# Revit family: Genie_Site_Telehandler_GTH12561
name_source: partatom
category: Site
units: mm (PartAtom-declared; Revit-internal decimal feet)

## family parameters
Always vertical = Yes
Cut with Voids When Loaded = No
OmniClass Number = 23.50.85.17
OmniClass Title = Telescoping Platforms
Part Type = Normal
Round Connector Dimension = Use Diameter
Shared = No
Work Plane-Based = No

## types (1)
- GTH-1256
    Assembly Code = E1030900
    AssetType = Fixed
    BIMObjectName = Genie_Site_Telehandler_GTH1256
    ClassificationName = Uniclass2015
    ClassificationValue = Pr_65_80_47_95
    Color = Grey & Blue
    Cost = 0 $
    Description = The Genie® GTH™-1256 telehandler delivers productivity with a large lifting capacity, high reach and compact maneuverability. And, this telehandler is built to perform, featuring a military-grade chassis design, standard Genie Quick-Attach™ system and auxiliary hydraulics. The right-side mount engine and a rear-mounted boom support design offers exceptional operator visibility.
    DocumentationCertificates = https://www.bimstore.co
    DocumentationInstallationGuide = https://www.bimstore.co
    DocumentationLiterature = https://www.bimstore.co
    DocumentationMaintenance = https://www.bimstore.co
    DocumentationTechnical = https://www.bimstore.co
    DurationUnit = Years
    ExpectedLife = 0
    Features = Ideal lifting applications in construction, landscaping and agriculture. Ideal for loading/unloading and moving/placing materials, as well as jobsite cleanup. Proportional frame-leveling chassis — pick up or place loads on up to 7˚ side slopes. Multi-function proportional joystick control for fast, precise load positioning. Full-time 4WD and 4WS
    Finish = Painted Steel
    IfcExportAs = IfcTransportElement
    IfcExportType = IfcTransportElementType
    Keynote = X
    Manufacturer = Genie
    ManufacturerName = Genie
    Material = Painted Steel
    Model = Genie - Telehandeler
    ModelNumber = GTH-1256
    ModelReference = Genie - Telehandeler
    NBSDescription = Vertical lifting platforms
    NBSObjectName = Genie - Vertical lifting platforms
    NBSReference = 90-80-65/350
    NominalDepth = 2590 mm
    NominalHeight = 2590 mm
    NominalLength = 6710 mm  [stored 22.0144 ft]
    ProductionYear = 2022
    ReplacementCost = 0
    Size = 2.59m x 2.59m x 6.71m
    Type Comments = GTH-1256
    TypeName = Genie - Telehandeler
    URL = http://www.genielift.co.uk
    WarrantyDurationLabor = 0
    WarrantyDurationParts = 0
    WarrantyDurationUnit = Years
    WarrantyGuarantorLabor = http://www.genielift.co.uk
    WarrantyGuarantorParts = http://www.genielift.co.uk
    _BSBibleVersion = 16
    _BimSpecGuid = 0
    _CurrentRevision = 1
    _DistributedBy = www.bimstore.co
    _ObjectUserGuide = https://www.bimstore.co

note: [stored X ft] marks values corroborated as IEEE doubles in the binary element streams (Revit-internal decimal feet)

## geometry (parser evidence)
native form markers: Sweep x41
no freeform markers — native parametric forms only
